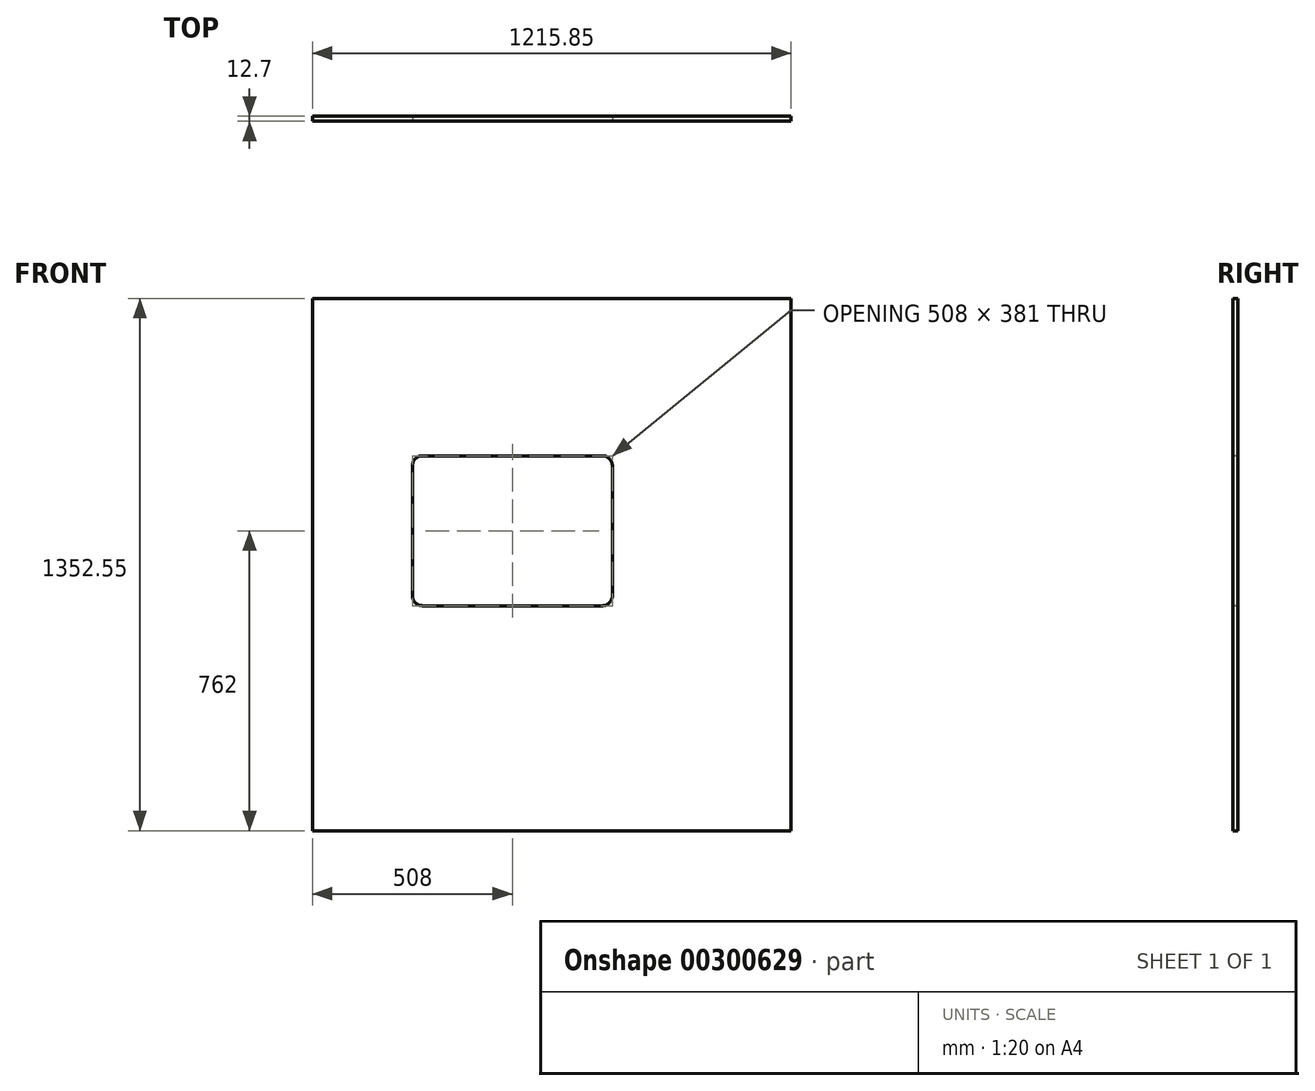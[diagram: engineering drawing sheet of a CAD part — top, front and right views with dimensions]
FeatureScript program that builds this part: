
annotation { "Feature Type Name" : "Feature", "Feature Type Description" : "" }
export const myFeature = defineFeature(function(context is Context, id is Id, definition is map)
    precondition{}
    {
        {
            var Q0;
            Q0=qCreatedBy(makeId("Front.planeOp"),FACE);
            var sketch = newSketch(context, id + "F0", { "sketchPlane" : qUnion([Q0])});
            skLineSegment(sketch, "E0.bottom", {"start": v(0, 0) * mm, "end": v(1215.85, 0) * mm});
            skLineSegment(sketch, "E0.top", {"start": v(0, 1352.55) * mm, "end": v(1215.85, 1352.55) * mm});
            skLineSegment(sketch, "E0.left", {"start": v(0, 0) * mm, "end": v(0, 1352.55) * mm});
            skLineSegment(sketch, "E0.right", {"start": v(1215.85, 0) * mm, "end": v(1215.85, 1352.55) * mm});
            skSolve(sketch);
        }
        {
            var Q0;
            Q0=makeQuery(id+"F0.imprint","IMPRINT",FACE,{"disambiguationData":[TD([[makeQuery(id+"F0.imprint","IMPRINT",EDGE,{"derivedFrom":sQuery(id+"F0.wireOp",EDGE,"E0.bottom")}),1.0]])]});
            extrude(context, id + "F1", {"entities" : qUnion([Q0]), "depth" : 12.7 * mm});
        }
        {
            var Q0;
            Q0=makeQuery(id+"F1.opExtrude","CAP_FACE",FACE,{"disambiguationData":[OSD([sQuery(id+"F0.wireOp",EDGE,"E0.bottom"),sQuery(id+"F0.wireOp",EDGE,"E0.top"),sQuery(id+"F0.wireOp",EDGE,"E0.left"),sQuery(id+"F0.wireOp",EDGE,"E0.right")])],"isStart":false});
            var sketch = newSketch(context, id + "F2", { "sketchPlane" : qUnion([Q0])});
            skLineSegment(sketch, "E1.bottom", {"start": v(736.6, 571.5) * mm, "end": v(279.4, 571.5) * mm});
            skLineSegment(sketch, "E1.top", {"start": v(736.6, 952.5) * mm, "end": v(279.4, 952.5) * mm});
            skLineSegment(sketch, "E1.left", {"start": v(762, 596.9) * mm, "end": v(762, 927.1) * mm});
            skLineSegment(sketch, "E1.right", {"start": v(254, 596.9) * mm, "end": v(254, 927.1) * mm});
            skPoint(sketch, "E1.middle", {"position": v(508, 762) * mm});
            skPoint(sketch, "E2.visualSharp", {"position": v(254, 952.5) * mm});
            skArc(sketch, "E2.filletArc", {"start": v(279.4, 952.5) * mm, "mid": v(261.44, 945.06) * mm, "end": v(254, 927.1) * mm});
            skPoint(sketch, "E3.visualSharp", {"position": v(254, 571.5) * mm});
            skArc(sketch, "E3.filletArc", {"start": v(254, 596.9) * mm, "mid": v(261.44, 578.94) * mm, "end": v(279.4, 571.5) * mm});
            skPoint(sketch, "E4.visualSharp", {"position": v(762, 571.5) * mm});
            skArc(sketch, "E4.filletArc", {"start": v(736.6, 571.5) * mm, "mid": v(754.56, 578.94) * mm, "end": v(762, 596.9) * mm});
            skPoint(sketch, "E5.visualSharp", {"position": v(762, 952.5) * mm});
            skArc(sketch, "E5.filletArc", {"start": v(762, 927.1) * mm, "mid": v(754.56, 945.06) * mm, "end": v(736.6, 952.5) * mm});
            skSolve(sketch);
        }
        {
            var Q0;
            Q0 = qSketchRegion(id + "F2", true);
            extrude(context, id + "F3", {"entities" : qUnion([Q0]), "operationType" : NewBodyOperationType.REMOVE, "endBound" : BoundingType.THROUGH_ALL, "oppositeDirection" : true, "depth" : 25.4 * mm});
        }
    });
